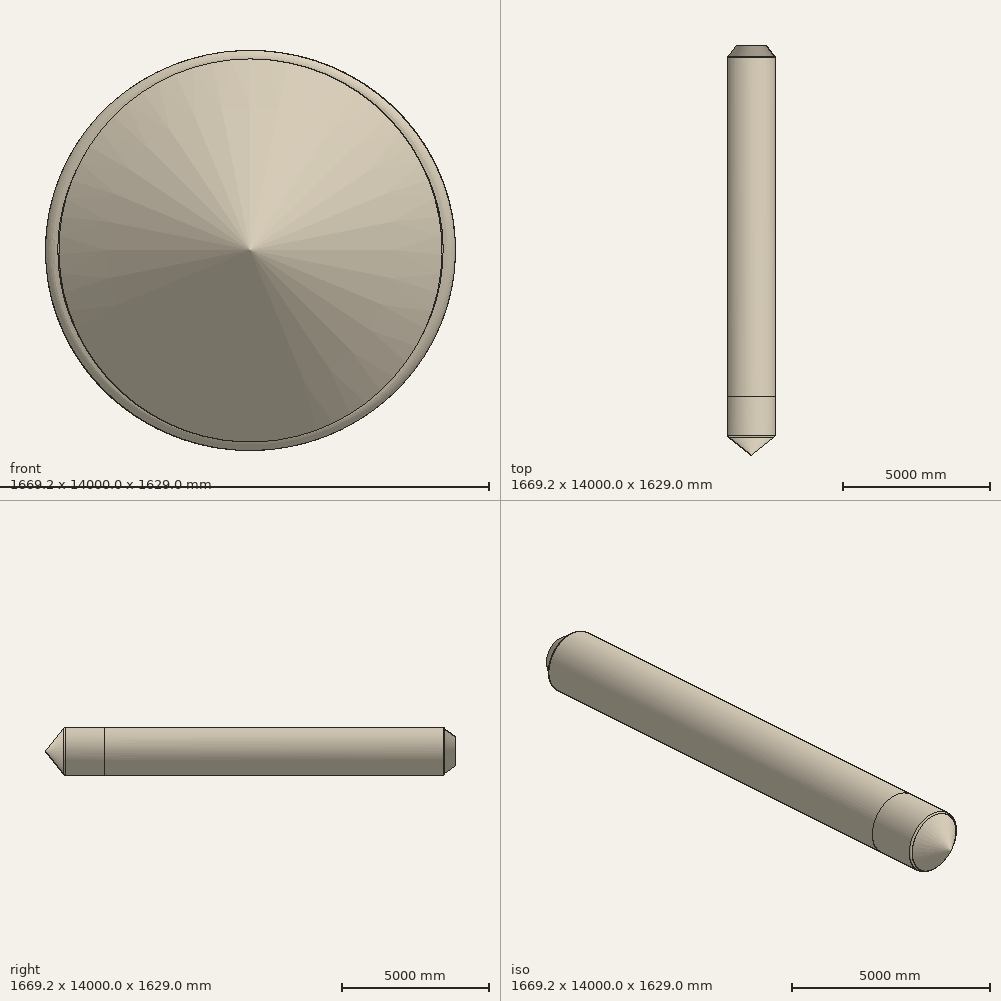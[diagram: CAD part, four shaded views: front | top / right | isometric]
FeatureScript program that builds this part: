
annotation { "Feature Type Name" : "Feature", "Feature Type Description" : "" }
export const myFeature = defineFeature(function(context is Context, id is Id, definition is map)
    precondition{}
    {
        {
            var Q0;
            Q0=qCreatedBy(makeId("Top.planeOp"),FACE);
            var sketch = newSketch(context, id + "F0", { "sketchPlane" : qUnion([Q0])});
            skLineSegment(sketch, "E0", {"start": v(-780, 625.78) * mm, "end": v(0, 0) * mm});
            skLineSegment(sketch, "E1", {"start": v(-780, 625.78) * mm, "end": v(0, 625.78) * mm});
            skLineSegment(sketch, "E2", {"start": v(0, 625.78) * mm, "end": v(0, 0) * mm});
            skLineSegment(sketch, "E3", {"start": v(780, 625.78) * mm, "end": v(-780, 625.78) * mm});
            skSolve(sketch);
        }
        {
            var Q0;
            Q0=makeQuery(id+"F0.imprint","IMPRINT",FACE,{"disambiguationData":[TD([[makeQuery(id+"F0.imprint","IMPRINT",EDGE,{"derivedFrom":sQuery(id+"F0.wireOp",EDGE,"E0")}),1.0]])]});
            var Q1;
            Q1=sQuery(id+"F0.wireOp",EDGE,"E2");
            revolve(context, id + "F1", {"entities" : qUnion([Q0]), "axis" : qUnion([Q1]), "revolveType" : RevolveType.FULL});
        }
        {
            var Q0;
            Q0=qCreatedBy(makeId("Front.planeOp"),FACE);
            cPlane(context, id + "F2", {"entities" : qUnion([Q0]), "cplaneType" : CPlaneType.OFFSET, "offset" : 2000 * mm, "oppositeDirection" : true, "width" : 150 * mm, "height" : 150 * mm});
        }
        {
            var Q0;
            Q0=qCreatedBy(id+"F2.planeOp",FACE);
            var sketch = newSketch(context, id + "F3", { "sketchPlane" : qUnion([Q0])});
            skEllipse(sketch, "E4", {"center": v(0, 0) * mm, "majorRadius": 814.5 * mm, "minorRadius": 834.62 * mm, "majorAxis": v(0, 1)});
            skSolve(sketch);
        }
        {
            var Q0;
            Q0=makeQuery(id+"F3.imprint","IMPRINT",FACE,{"disambiguationData":[TD([[makeQuery(id+"F3.imprint","IMPRINT",EDGE,{"derivedFrom":sQuery(id+"F3.wireOp",EDGE,"E4")}),1.0]])]});
            extrude(context, id + "F4", {"entities" : qUnion([Q0]), "depth" : 1370 * mm});
        }
        {
            var Q0;
            Q0=makeQuery(id+"F4.opExtrude","CAP_EDGE",EDGE,{"disambiguationData":[OSD([sQuery(id+"F3.wireOp",EDGE,"E4")])],"isStart":false});
            fillet(context, id + "F5", {"entities" : qUnion([Q0]), "radius" : 50 * mm, "tangentPropagation" : true, "allowEdgeOverflow" : false});
        }
        {
            var Q0;
            Q0=makeQuery(id+"F4.opExtrude","CAP_FACE",FACE,{"disambiguationData":[OSD([sQuery(id+"F3.wireOp",EDGE,"E4")])],"isStart":true});
            extrude(context, id + "F6", {"entities" : qUnion([Q0]), "depth" : 11630 * mm});
        }
        {
            var Q0;
            Q0=makeQuery(id+"F6.opExtrude","CAP_EDGE",EDGE,{"disambiguationData":[OSD([sQuery(id+"F3.wireOp",EDGE,"E4")])],"isStart":false});
            fillet(context, id + "F7", {"entities" : qUnion([Q0]), "radius" : 50 * mm, "tangentPropagation" : true, "allowEdgeOverflow" : false});
        }
        {
            var Q0;
            Q0=qCreatedBy(makeId("Front.planeOp"),FACE);
            cPlane(context, id + "F8", {"entities" : qUnion([Q0]), "cplaneType" : CPlaneType.OFFSET, "offset" : 14000 * mm, "oppositeDirection" : true, "width" : 150 * mm, "height" : 150 * mm});
        }
        {
            var Q0;
            Q0=qCreatedBy(id+"F8.planeOp",FACE);
            var sketch = newSketch(context, id + "F9", { "sketchPlane" : qUnion([Q0])});
            skCircle(sketch, "E5", {"center": v(0, 0) * mm, "radius": 501.86 * mm});
            skSolve(sketch);
        }
        {
            var Q0;
            Q0=makeQuery(id+"F6.opExtrude","CAP_FACE",FACE,{"disambiguationData":[OSD([sQuery(id+"F3.wireOp",EDGE,"E4")])],"isStart":false});
            var Q1;
            Q1=makeQuery(id+"F9.imprint","IMPRINT",FACE,{"disambiguationData":[TD([[makeQuery(id+"F9.imprint","IMPRINT",EDGE,{"derivedFrom":sQuery(id+"F9.wireOp",EDGE,"E5")}),1.0]])]});
            loft(context, id + "F10", {"sheetProfilesArray" : [{ "sheetProfileEntities" : qUnion([Q0]) }, { "sheetProfileEntities" : qUnion([Q1]) }]});
        }
    });
